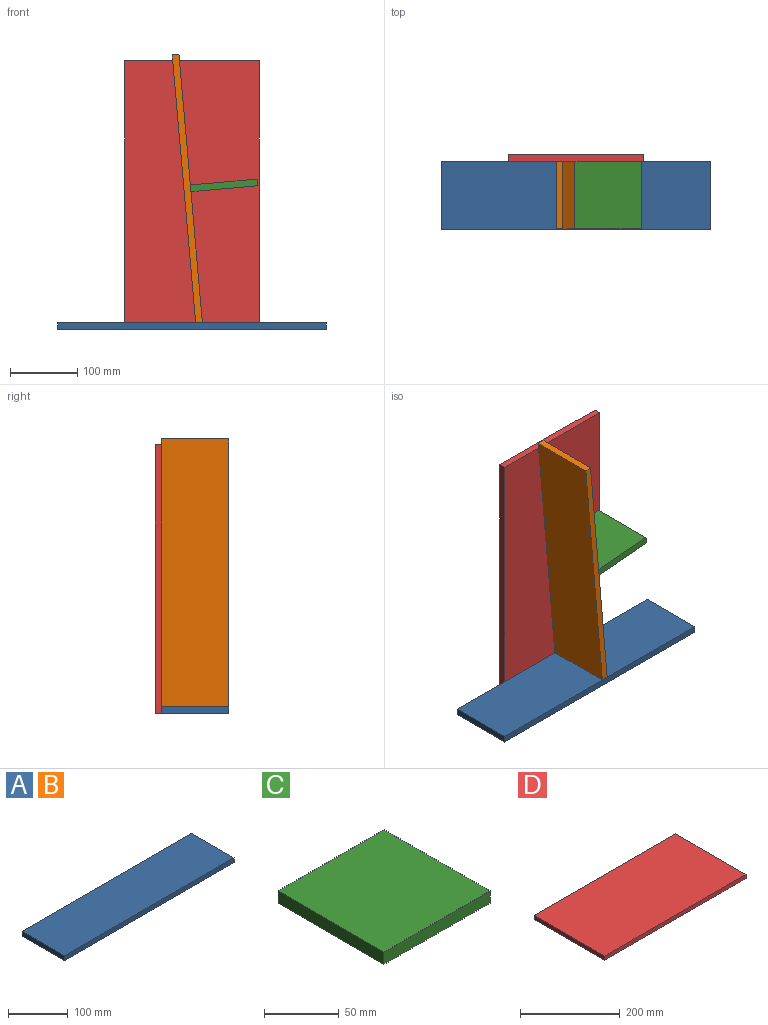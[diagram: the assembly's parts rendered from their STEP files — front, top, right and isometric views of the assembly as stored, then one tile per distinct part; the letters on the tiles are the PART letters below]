
ASSEMBLY  parts=4 mates=4
PART A: 6 faces, bbox 400x100x10 mm
  f0: plane 400x10mm, normal (0,1,0), area 4000mm2, adj f1,f3,f4,f5
  f1: plane 100x10mm, normal (-1,0,0), area 1000mm2, adj f0,f2,f4,f5
  f2: plane 400x10mm, normal (0,-1,0), area 4000mm2, adj f1,f3,f4,f5
  f3: plane 100x10mm, normal (1,0,0), area 1000mm2, adj f0,f2,f4,f5
  f4: plane 400x100mm, normal (0,0,1), area 40000mm2, adj f0,f1,f2,f3
  f5: plane 400x100mm, normal (0,0,-1), area 40000mm2, adj f0,f1,f2,f3
PART B: same geometry as A
PART C: 6 faces, bbox 100x100x10 mm
  f0: plane 100x10mm, normal (0,1,0), area 1000mm2, adj f1,f3,f4,f5
  f1: plane 100x10mm, normal (-1,0,0), area 1000mm2, adj f0,f2,f4,f5
  f2: plane 100x10mm, normal (0,-1,0), area 1000mm2, adj f1,f3,f4,f5
  f3: plane 100x10mm, normal (1,0,0), area 1000mm2, adj f0,f2,f4,f5
  f4: plane 100x100mm, normal (0,0,1), area 10000mm2, adj f0,f1,f2,f3
  f5: plane 100x100mm, normal (0,0,-1), area 10000mm2, adj f0,f1,f2,f3
PART D: 6 faces, bbox 400x200x10 mm
  f0: plane 400x10mm, normal (0,1,0), area 4000mm2, adj f1,f3,f4,f5
  f1: plane 200x10mm, normal (-1,0,0), area 2000mm2, adj f0,f2,f4,f5
  f2: plane 400x10mm, normal (0,-1,0), area 4000mm2, adj f1,f3,f4,f5
  f3: plane 200x10mm, normal (1,0,0), area 2000mm2, adj f0,f2,f4,f5
  f4: plane 400x200mm, normal (0,0,1), area 80000mm2, adj f0,f1,f2,f3
  f5: plane 400x200mm, normal (0,0,-1), area 80000mm2, adj f0,f1,f2,f3
PLACE A t=(-90,-113.42,10.76)mm
PLACE B rot(axis=(0,-1,0),95deg) t=(-97,-113.42,215.53)mm
PLACE C rot(axis=(0,-1,0),5deg) t=(-42.21,-113.42,220.33)mm
PLACE D rot(axis=(0.58,0.58,-0.58),120deg) t=(-90,-58.42,205.76)mm
MATE parallel D.f3 <-> A.f5  axis (0,0,-1) through (-90,-58.42,5.76)mm
MATE parallel A.f3 <-> D.f0  axis (1,0,0) through (110,-113.42,10.76)mm
MATE planar C.f1 <-> B.f5  axis (-1,0,-0.09) through (-92.02,-113.42,215.97)mm
MATE planar D.f4 <-> A.f0  axis (0,-1,0) through (-90,-63.42,205.76)mm
